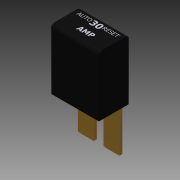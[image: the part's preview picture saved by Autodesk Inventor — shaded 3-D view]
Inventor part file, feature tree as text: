
AUTODESK INVENTOR PART (.ipt)
format: ipt  version: 2016 SP1 (Build 200210100, 210)  size: 482,304 bytes
history: native  units: in
note: dims shown in document units (in); Inventor stores cm internally (conversion verified against a paired STEP export)
features: sketch x6, extrude x4, plane x3, emboss x2, fillet x1, mirror x1
ambient origin geometry x8: Origin, YZ Plane, XZ Plane, XY Plane, X Axis, Y Axis, Z Axis, Center Point
bodies: Solid1 (feature_tree)
feature tree (17):
  extrude  "Extrusion1"  Depth=0.39in
  fillet  "Fillet1"  Radius=0.78in
  extrude  "Extrusion3"  Depth=0.212in
  extrude  "Extrusion4"  Depth=0.0585in
  extrude  "Extrusion5"  Depth=0.57in TaperAngle=0.0deg
  plane  "Work Plane1"
  mirror  "Mirror1"
  plane  "Work Plane2"
  emboss  "Emboss1"
  plane  "Work Plane4"
  emboss  "Emboss3"
  sketch  "Sketch1"  dims[d0=0.62in d1=0.39in d2=0.78in d3=0.0in]
  sketch  "Sketch2"  dims[d4=0.01in d5=0.05in d6=0.212in]
  sketch  "Sketch3"  dims[d8=0.031in d13=0.0585in]
  sketch  "Sketch4"  dims[d14=0.57in d15=0.0in d16=0.57in d17=0.0in]
  sketch  "Sketch6"  dims[d18=0.023in]
  sketch  "Sketch8"  dims[d19=0.023in d20=0.023in d21=0.57in d22=0.0in d26=0.1875in d27=0.0001in d28=0.0in d32=0.1875in d33=0.0001in d34=0.0in]
